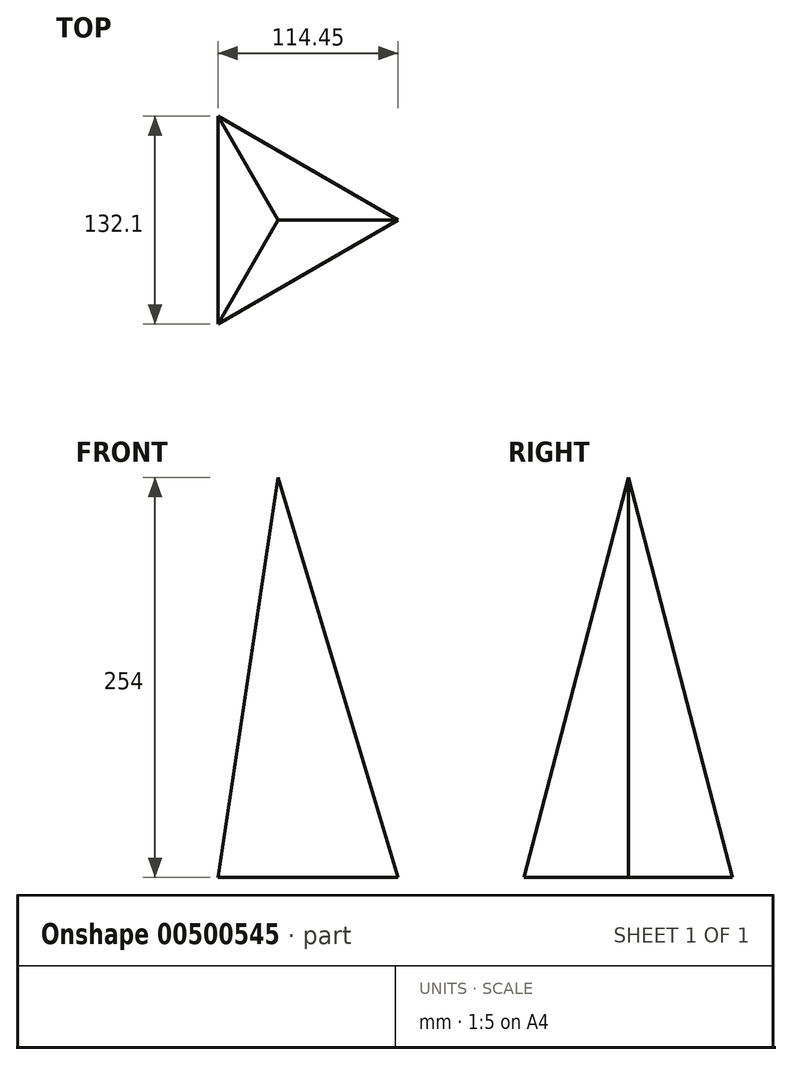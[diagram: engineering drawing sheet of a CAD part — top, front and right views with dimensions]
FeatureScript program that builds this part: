
annotation { "Feature Type Name" : "Feature", "Feature Type Description" : "" }
export const myFeature = defineFeature(function(context is Context, id is Id, definition is map)
    precondition{}
    {
        {
            var Q0;
            Q0=qCreatedBy(makeId("Top.planeOp"),FACE);
            var sketch = newSketch(context, id + "F0", { "sketchPlane" : qUnion([Q0])});
            skCircle(sketch, "E0.cCircle", {"center": v(0, 0) * mm, "radius": 76.27 * mm, "construction": true});
            skLineSegment(sketch, "E0.0", {"start": v(-38.18, 66.02) * mm, "end": v(76.27, 0.06) * mm});
            skLineSegment(sketch, "E0.1", {"start": v(76.27, 0.06) * mm, "end": v(-38.08, -66.08) * mm});
            skLineSegment(sketch, "E0.2", {"start": v(-38.08, -66.08) * mm, "end": v(-38.18, 66.02) * mm});
            skSolve(sketch);
        }
        {
            var Q0;
            Q0=qCreatedBy(makeId("Top.planeOp"),FACE);
            cPlane(context, id + "F1", {"entities" : qUnion([Q0]), "cplaneType" : CPlaneType.OFFSET, "offset" : 254 * mm, "width" : 152.4 * mm, "height" : 152.4 * mm});
        }
        {
            var Q0;
            Q0=qCreatedBy(id+"F1.planeOp",FACE);
            var sketch = newSketch(context, id + "F2", { "sketchPlane" : qUnion([Q0])});
            skPoint(sketch, "E1", {"position": v(0, 0) * mm});
            skSolve(sketch);
        }
        {
            var Q0;
            Q0=makeQuery(id+"F0.imprint","IMPRINT",FACE,{"disambiguationData":[TD([[makeQuery(id+"F0.imprint","IMPRINT",EDGE,{"derivedFrom":sQuery(id+"F0.wireOp",EDGE,"E0.0")}),-1.0]])]});
            var Q1;
            Q1=sQuery(id+"F2.wireOp",VERTEX,"E1");
            loft(context, id + "F3", {"sheetProfilesArray" : [{ "sheetProfileEntities" : qUnion([Q0]) }, { "sheetProfileEntities" : qUnion([Q1]) }]});
        }
    });
